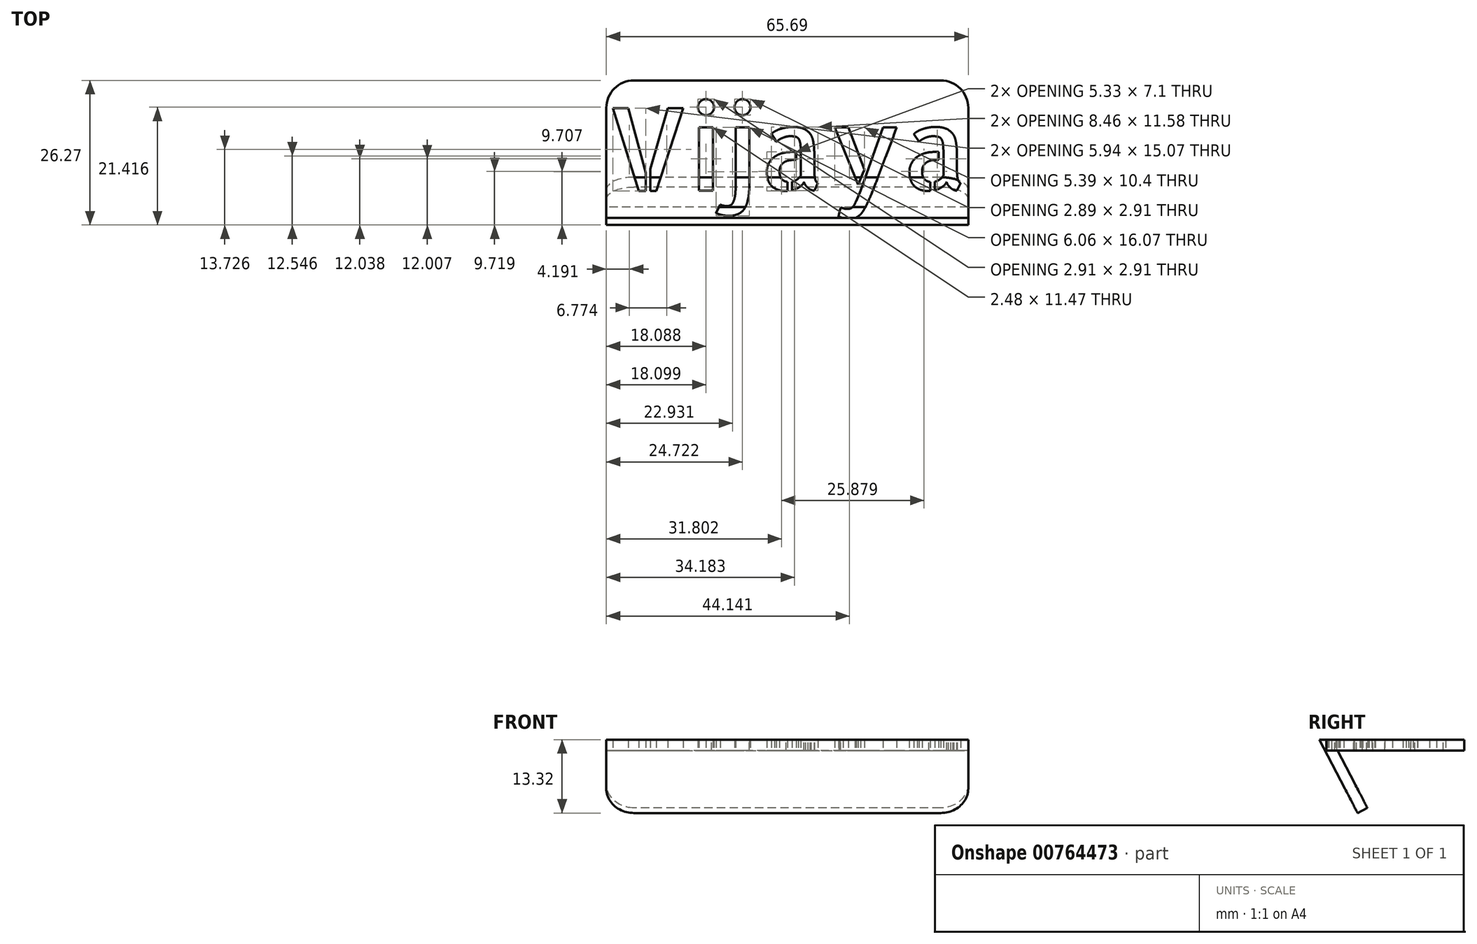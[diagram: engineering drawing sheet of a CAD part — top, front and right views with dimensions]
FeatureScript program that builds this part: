
annotation { "Feature Type Name" : "Feature", "Feature Type Description" : "" }
export const myFeature = defineFeature(function(context is Context, id is Id, definition is map)
    precondition{}
    {
        {
            var Q0;
            Q0=qCreatedBy(makeId("Top.planeOp"),FACE);
            var sketch = newSketch(context, id + "F0", { "sketchPlane" : qUnion([Q0])});
            skLineSegment(sketch, "E0.bottom", {"start": v(-23.58, 12.5) * mm, "end": v(42.1, 12.5) * mm});
            skLineSegment(sketch, "E0.top", {"start": v(-23.58, -12.5) * mm, "end": v(42.1, -12.5) * mm});
            skLineSegment(sketch, "E0.left", {"start": v(-23.58, 12.5) * mm, "end": v(-23.58, -12.5) * mm});
            skLineSegment(sketch, "E0.right", {"start": v(42.1, 12.5) * mm, "end": v(42.1, -12.5) * mm});
            skText(sketch, "E1", { "text": "Vijaya", "fontName": "AllertaStencil-Regular.ttf"});
            const initialGuessF0  = {"E1": [-0.02358, -0.0075, 1, 0, 0.015]};
            skSetInitialGuess(sketch, initialGuessF0);
            skSolve(sketch);
        }
        {
            var Q0;
            Q0=makeQuery(id+"F0.imprint","IMPRINT",FACE,{"disambiguationData":[TD([[makeQuery(id+"F0.imprint","IMPRINT",EDGE,{"derivedFrom":sQuery(id+"F0.wireOp",EDGE,"E0.bottom")}),-1.0]])]});
            extrude(context, id + "F1", {"entities" : qUnion([Q0]), "depth" : 2 * mm, "offsetDistance" : 25 * mm});
        }
        {
            var Q0;
            {var subQ0=sQuery(id+"F0.wireOp",EDGE,"E0.left");Q0=makeQuery(id+"FYEOEdhl7jzHk82_2.opBoolean","MERGE",FACE,{"derivedFrom":[makeQuery(id+"F1.opExtrude","SWEPT_FACE",FACE,{"disambiguationData":[OSD([subQ0])]}),makeQuery(id+"FOv1BJgTRWeWuMw_1.opExtrude","CAP_FACE",FACE,{"disambiguationData":[OSD([sQuery(id+"F0.wireOp",EDGE,"E0.bottom"),subQ0,sQuery(id+"Fjco5yBOxZZxTCI_1.wireOp",EDGE,"TpTMtmOo-qoIM-rLEy-p7IH-mKgsBanMGF23"),sQuery(id+"Fjco5yBOxZZxTCI_1.wireOp",EDGE,"Ja6BvVoQ-cpFi-Lcom-cL8s-5xC4kZiynyNl"),sQuery(id+"Fjco5yBOxZZxTCI_1.wireOp",EDGE,"utNyaJ8P-FD6r-AD7x-tpFW-fHytfVhziHLl"),sQuery(id+"Fjco5yBOxZZxTCI_1.wireOp",EDGE,"xGzW29bi-H5H8-ObLh-gdKj-mSPkAtMAUUzO")])],"isStart":true})]});}
            var sketch = newSketch(context, id + "F2", { "sketchPlane" : qUnion([Q0])});
            skLineSegment(sketch, "E2", {"start": v(11.52, 2) * mm, "end": v(5.09, -10.4) * mm});
            skLineSegment(sketch, "E3", {"start": v(5.09, -10.4) * mm, "end": v(6.87, -11.32) * mm});
            skLineSegment(sketch, "E4", {"start": v(6.87, -11.32) * mm, "end": v(13.77, 2) * mm});
            skLineSegment(sketch, "E5", {"start": v(13.77, 2) * mm, "end": v(11.52, 2) * mm});
            skSolve(sketch);
        }
        {
            var Q0;
            {var subQ4=sQuery(id+"F2.wireOp",EDGE,"E3");Q0=makeQuery(id+"F2.imprint","IMPRINT",FACE,{"disambiguationData":[TD([[makeQuery(id+"F2.imprint","IMPRINT",EDGE,{"derivedFrom":subQ4}),1.0]])]});}
            var Q1;
            Q1=makeQuery(id+"F1.opExtrude","SWEPT_FACE",FACE,{"disambiguationData":[OSD([sQuery(id+"F0.wireOp",EDGE,"E0.right")])]});
            extrude(context, id + "F3", {"entities" : qUnion([Q0]), "endBound" : BoundingType.UP_TO_SURFACE, "oppositeDirection" : true, "depth" : 75 * mm, "endBoundEntityFace" : qUnion([Q1]), "offsetDistance" : 25 * mm});
        }
        {
            var Q0;
            Q0=makeQuery(id+"F1.opExtrude","SWEPT_EDGE",EDGE,{"disambiguationData":[OSD([sQuery(id+"F0.wireOp",EDGE,"E0.bottom"),sQuery(id+"F0.wireOp",EDGE,"E0.left")])]});
            var Q1;
            Q1=makeQuery(id+"F1.opExtrude","SWEPT_EDGE",EDGE,{"disambiguationData":[OSD([sQuery(id+"F0.wireOp",EDGE,"E0.bottom"),sQuery(id+"F0.wireOp",EDGE,"E0.right")])]});
            var Q2;
            Q2=makeQuery(id+"F3.opExtrude","CAP_EDGE",EDGE,{"disambiguationData":[OSD([sQuery(id+"F2.wireOp",EDGE,"E3")])],"isStart":false});
            var Q3;
            Q3=makeQuery(id+"F3.opExtrude","CAP_EDGE",EDGE,{"disambiguationData":[OSD([sQuery(id+"F2.wireOp",EDGE,"E3")])],"isStart":true});
            var Q4;
            Q4=makeQuery(id+"F3.opExtrude","TWEAK_EDGE",EDGE,{"derivedFrom":[makeQuery(id+"F1.opExtrude","SWEPT_FACE",FACE,{"disambiguationData":[OSD([sQuery(id+"F0.wireOp",EDGE,"E0.right")])]}),makeQuery(id+"F2.imprint","IMPRINT",EDGE,{"derivedFrom":sQuery(id+"F2.wireOp",EDGE,"E3")})]});
            fillet(context, id + "F4", {"entities" : qUnion([Q0, Q1, Q2, Q3, Q4]), "radius" : 5 * mm, "tangentPropagation" : true, "allowEdgeOverflow" : false});
        }
    });
